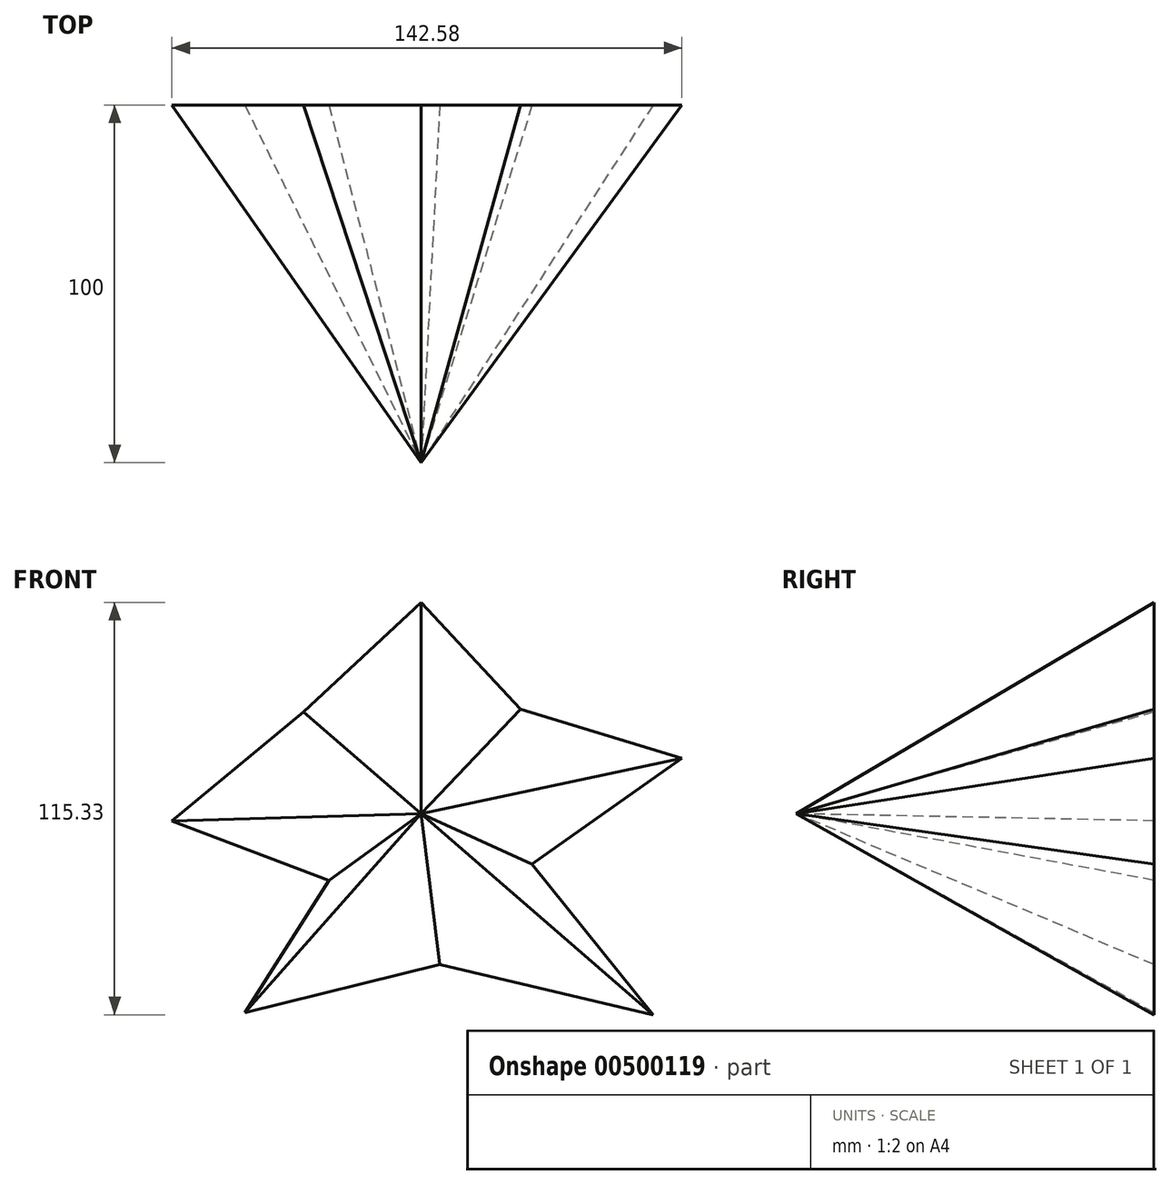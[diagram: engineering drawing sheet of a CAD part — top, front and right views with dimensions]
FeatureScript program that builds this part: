
annotation { "Feature Type Name" : "Feature", "Feature Type Description" : "" }
export const myFeature = defineFeature(function(context is Context, id is Id, definition is map)
    precondition{}
    {
        {
            var Q0;
            Q0=qCreatedBy(makeId("Front.planeOp"),FACE);
            var sketch = newSketch(context, id + "F0", { "sketchPlane" : qUnion([Q0])});
            skLineSegment(sketch, "E0", {"start": v(-33, 24.24) * mm, "end": v(0, 54.94) * mm});
            skLineSegment(sketch, "E1", {"start": v(0, 54.94) * mm, "end": v(27.8, 25.06) * mm});
            skLineSegment(sketch, "E2", {"start": v(27.8, 25.06) * mm, "end": v(72.87, 11.33) * mm});
            skLineSegment(sketch, "E3", {"start": v(72.87, 11.33) * mm, "end": v(30.98, -18.22) * mm});
            skLineSegment(sketch, "E4", {"start": v(30.98, -18.22) * mm, "end": v(64.84, -60.39) * mm});
            skLineSegment(sketch, "E5", {"start": v(64.84, -60.39) * mm, "end": v(5.16, -46.33) * mm});
            skLineSegment(sketch, "E6", {"start": v(5.16, -46.33) * mm, "end": v(-49.34, -59.82) * mm});
            skLineSegment(sketch, "E7", {"start": v(-49.34, -59.82) * mm, "end": v(-25.82, -22.8) * mm});
            skLineSegment(sketch, "E8", {"start": v(-25.82, -22.8) * mm, "end": v(-69.71, -6.17) * mm});
            skLineSegment(sketch, "E9", {"start": v(-69.71, -6.17) * mm, "end": v(-33, 24.24) * mm});
            skSolve(sketch);
        }
        {
            var Q0;
            Q0=qCreatedBy(makeId("Front.planeOp"),FACE);
            cPlane(context, id + "F1", {"entities" : qUnion([Q0]), "cplaneType" : CPlaneType.OFFSET, "offset" : 100 * mm, "width" : 150 * mm, "height" : 150 * mm});
        }
        {
            var Q0;
            Q0=qCreatedBy(id+"F1.planeOp",FACE);
            var sketch = newSketch(context, id + "F2", { "sketchPlane" : qUnion([Q0])});
            skPoint(sketch, "E10", {"position": v(0, -4.19) * mm});
            skSolve(sketch);
        }
        {
            var Q0;
            Q0=makeQuery(id+"F0.imprint","IMPRINT",FACE,{"disambiguationData":[TD([[makeQuery(id+"F0.imprint","IMPRINT",EDGE,{"derivedFrom":sQuery(id+"F0.wireOp",EDGE,"E0")}),-1.0]])]});
            var Q1;
            Q1=sQuery(id+"F2.wireOp",VERTEX,"E10");
            loft(context, id + "F3", {"sheetProfilesArray" : [{ "sheetProfileEntities" : qUnion([Q0]) }, { "sheetProfileEntities" : qUnion([Q1]) }]});
        }
    });
